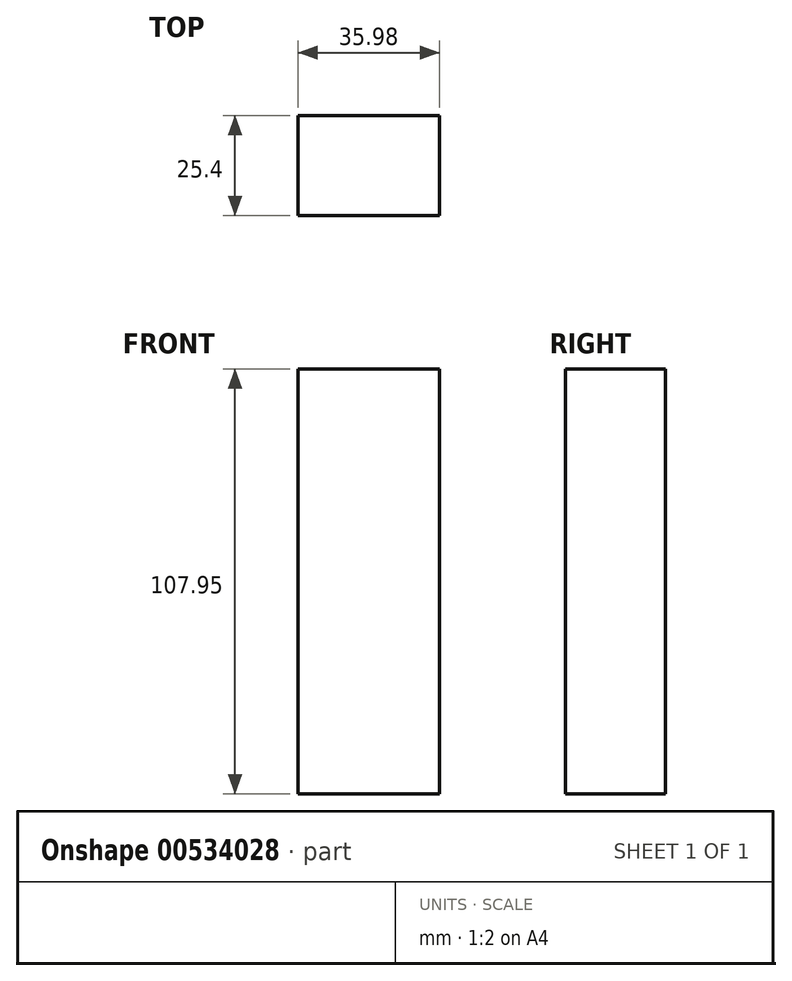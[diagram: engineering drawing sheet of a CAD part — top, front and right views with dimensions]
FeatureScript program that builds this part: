
annotation { "Feature Type Name" : "Feature", "Feature Type Description" : "" }
export const myFeature = defineFeature(function(context is Context, id is Id, definition is map)
    precondition{}
    {
        {
            var Q0;
            Q0=qCreatedBy(makeId("Front.planeOp"),FACE);
            var sketch = newSketch(context, id + "F0", { "sketchPlane" : qUnion([Q0])});
            skLineSegment(sketch, "E0.bottom", {"start": v(-45.24, 49.68) * mm, "end": v(-9.26, 49.68) * mm});
            skLineSegment(sketch, "E0.top", {"start": v(-45.24, -58.27) * mm, "end": v(-9.26, -58.27) * mm});
            skLineSegment(sketch, "E0.left", {"start": v(-45.24, 49.68) * mm, "end": v(-45.24, -58.27) * mm});
            skLineSegment(sketch, "E0.right", {"start": v(-9.26, 49.68) * mm, "end": v(-9.26, -58.27) * mm});
            skSolve(sketch);
        }
        {
            var Q0;
            Q0 = qSketchRegion(id + "F0", true);
            extrude(context, id + "F1", {"entities" : qUnion([Q0]), "depth" : 25.4 * mm, "offsetDistance" : 25.4 * mm});
        }
    });
